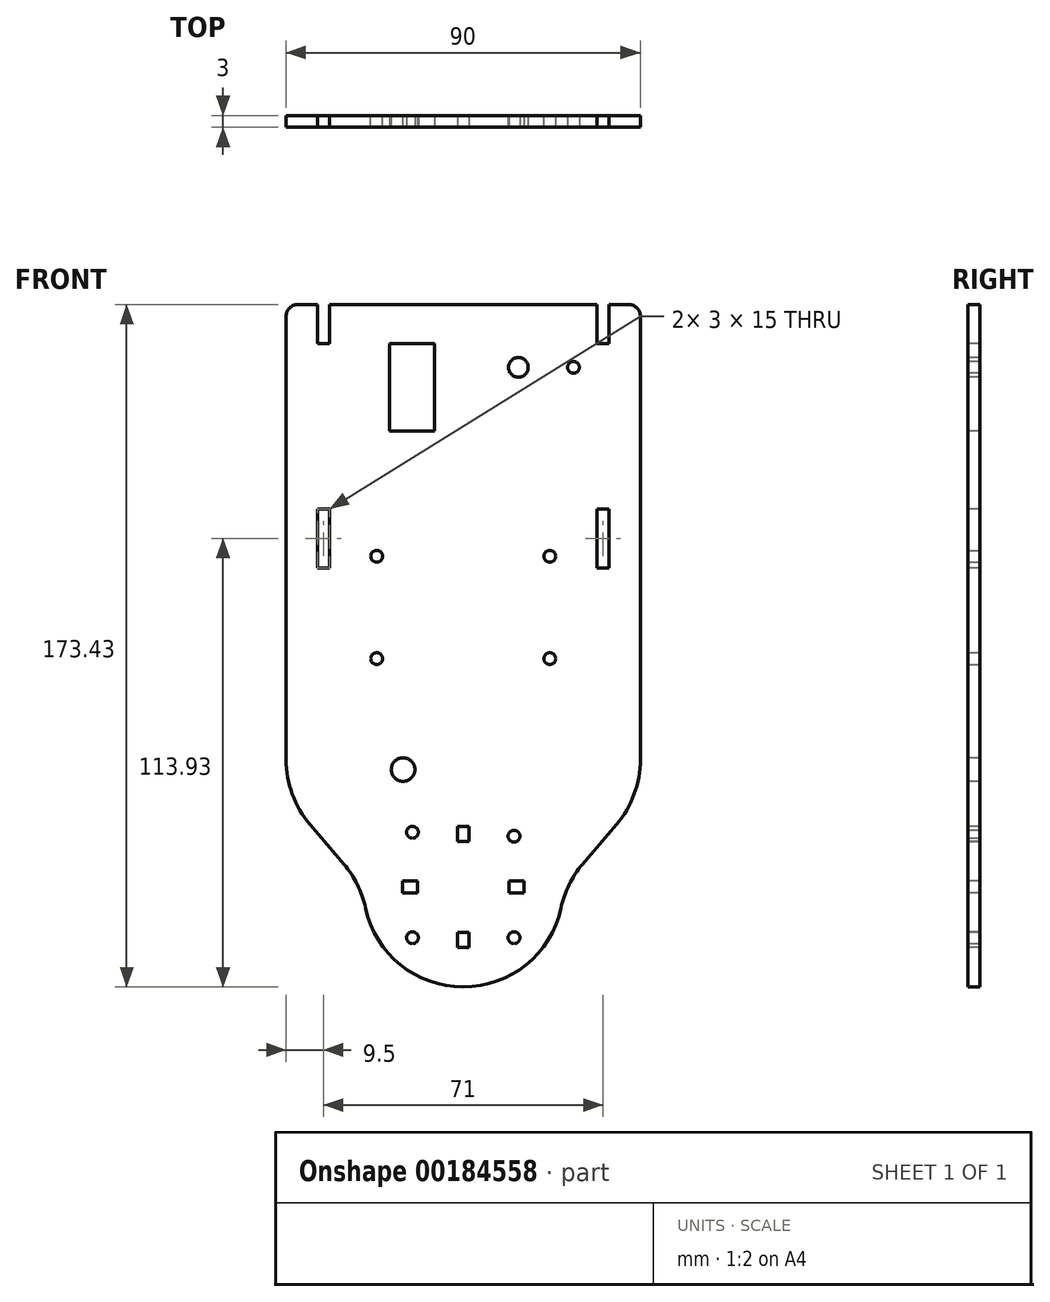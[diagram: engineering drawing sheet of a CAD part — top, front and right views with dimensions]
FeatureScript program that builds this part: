
annotation { "Feature Type Name" : "Feature", "Feature Type Description" : "" }
export const myFeature = defineFeature(function(context is Context, id is Id, definition is map)
    precondition{}
    {
        {
            var Q0;
            Q0=qCreatedBy(makeId("Front.planeOp"),FACE);
            var sketch = newSketch(context, id + "F0", { "sketchPlane" : qUnion([Q0])});
            skLineSegment(sketch, "E0.bottom", {"start": v(0, 0) * mm, "end": v(-90, 0) * mm});
            skLineSegment(sketch, "E0.top", {"start": v(0, 125) * mm, "end": v(-90, 125) * mm});
            skLineSegment(sketch, "E0.left", {"start": v(0, 0) * mm, "end": v(0, 125) * mm});
            skLineSegment(sketch, "E0.right", {"start": v(-90, 0) * mm, "end": v(-90, 125) * mm});
            skLineSegment(sketch, "E1", {"start": v(-90, 0) * mm, "end": v(-45, -70) * mm});
            skLineSegment(sketch, "E2", {"start": v(-45, -70) * mm, "end": v(0, 0) * mm});
            skSolve(sketch);
        }
        {
            var Q0;
            Q0=makeQuery(id+"F0.imprint","IMPRINT",FACE,{"disambiguationData":[TD([[makeQuery(id+"F0.imprint","IMPRINT",EDGE,{"derivedFrom":sQuery(id+"F0.wireOp",EDGE,"E0.bottom")}),-1.0]])]});
            var Q1;
            Q1=makeQuery(id+"F0.imprint","IMPRINT",FACE,{"disambiguationData":[TD([[makeQuery(id+"F0.imprint","IMPRINT",EDGE,{"derivedFrom":sQuery(id+"F0.wireOp",EDGE,"E0.bottom")}),1.0]])]});
            extrude(context, id + "F1", {"entities" : qUnion([Q0, Q1]), "depth" : 3 * mm});
        }
        {
            var Q0;
            Q0=makeQuery(id+"F1.opExtrude","CAP_FACE",FACE,{"disambiguationData":[OSD([sQuery(id+"F0.wireOp",EDGE,"E0.top"),sQuery(id+"F0.wireOp",EDGE,"E0.left"),sQuery(id+"F0.wireOp",EDGE,"E0.right"),sQuery(id+"F0.wireOp",EDGE,"E1"),sQuery(id+"F0.wireOp",EDGE,"E2")])],"isStart":false});
            var sketch = newSketch(context, id + "F2", { "sketchPlane" : qUnion([Q0])});
            skLineSegment(sketch, "E3.bottom", {"start": v(-8, 130) * mm, "end": v(-11, 130) * mm});
            skLineSegment(sketch, "E3.top", {"start": v(-8, 115) * mm, "end": v(-11, 115) * mm});
            skLineSegment(sketch, "E3.left", {"start": v(-11, 130) * mm, "end": v(-11, 115) * mm});
            skLineSegment(sketch, "E3.right", {"start": v(-8, 130) * mm, "end": v(-8, 115) * mm});
            skLineSegment(sketch, "E4.bottom", {"start": v(-8, 73) * mm, "end": v(-11, 73) * mm});
            skLineSegment(sketch, "E4.top", {"start": v(-8, 58) * mm, "end": v(-11, 58) * mm});
            skLineSegment(sketch, "E4.left", {"start": v(-8, 73) * mm, "end": v(-8, 58) * mm});
            skLineSegment(sketch, "E4.right", {"start": v(-11, 73) * mm, "end": v(-11, 58) * mm});
            skLineSegment(sketch, "E5.bottom", {"start": v(-79, 130) * mm, "end": v(-82, 130) * mm});
            skLineSegment(sketch, "E5.top", {"start": v(-79, 115) * mm, "end": v(-82, 115) * mm});
            skLineSegment(sketch, "E5.left", {"start": v(-79, 130) * mm, "end": v(-79, 115) * mm});
            skLineSegment(sketch, "E5.right", {"start": v(-82, 130) * mm, "end": v(-82, 115) * mm});
            skLineSegment(sketch, "E6.bottom", {"start": v(-79, 73) * mm, "end": v(-82, 73) * mm});
            skLineSegment(sketch, "E6.top", {"start": v(-79, 58) * mm, "end": v(-82, 58) * mm});
            skLineSegment(sketch, "E6.left", {"start": v(-79, 73) * mm, "end": v(-79, 58) * mm});
            skLineSegment(sketch, "E6.right", {"start": v(-82, 73) * mm, "end": v(-82, 58) * mm});
            skLineSegment(sketch, "E7", {"start": v(-79, 58) * mm, "end": v(-11, 58) * mm});
            skLineSegment(sketch, "E8.bottom", {"start": v(-40, 58) * mm, "end": v(-35, 58) * mm});
            skLineSegment(sketch, "E8.top", {"start": v(-40, 55) * mm, "end": v(-35, 55) * mm});
            skLineSegment(sketch, "E8.left", {"start": v(-40, 58) * mm, "end": v(-40, 55) * mm});
            skLineSegment(sketch, "E8.right", {"start": v(-35, 58) * mm, "end": v(-35, 55) * mm});
            skLineSegment(sketch, "E9", {"start": v(-45, 58) * mm, "end": v(-45, 63.12) * mm});
            skPoint(sketch, "E9.endSnap0", {"position": v(-45, 58) * mm});
            skLineSegment(sketch, "E10.bottom", {"start": v(-50, 58) * mm, "end": v(-55, 58) * mm});
            skLineSegment(sketch, "E10.top", {"start": v(-50, 55) * mm, "end": v(-55, 55) * mm});
            skLineSegment(sketch, "E10.left", {"start": v(-50, 58) * mm, "end": v(-50, 55) * mm});
            skLineSegment(sketch, "E10.right", {"start": v(-55, 58) * mm, "end": v(-55, 55) * mm});
            skSolve(sketch);
        }
        {
            var Q0;
            Q0=makeQuery(id+"F1.opExtrude","CAP_FACE",FACE,{"disambiguationData":[OSD([sQuery(id+"F0.wireOp",EDGE,"E0.top"),sQuery(id+"F0.wireOp",EDGE,"E0.left"),sQuery(id+"F0.wireOp",EDGE,"E0.right"),sQuery(id+"F0.wireOp",EDGE,"E1"),sQuery(id+"F0.wireOp",EDGE,"E2")])],"isStart":false});
            var sketch = newSketch(context, id + "F3", { "sketchPlane" : qUnion([Q0])});
            skLineSegment(sketch, "E11.bottom", {"start": v(-63.75, 115) * mm, "end": v(-52.25, 115) * mm});
            skLineSegment(sketch, "E11.top", {"start": v(-63.75, 92.8) * mm, "end": v(-52.25, 92.8) * mm});
            skLineSegment(sketch, "E11.left", {"start": v(-63.75, 115) * mm, "end": v(-63.75, 92.8) * mm});
            skLineSegment(sketch, "E11.right", {"start": v(-52.25, 115) * mm, "end": v(-52.25, 92.8) * mm});
            skCircle(sketch, "E12", {"center": v(-58, 117) * mm, "radius": 1 * mm});
            skCircle(sketch, "E13", {"center": v(-58, 90.8) * mm, "radius": 1 * mm});
            skLineSegment(sketch, "E14", {"start": v(-59, 117) * mm, "end": v(-59, 115) * mm});
            skLineSegment(sketch, "E15", {"start": v(-57, 117) * mm, "end": v(-57, 115) * mm});
            skLineSegment(sketch, "E16", {"start": v(-59, 90.8) * mm, "end": v(-59, 92.8) * mm});
            skLineSegment(sketch, "E17", {"start": v(-57, 92.8) * mm, "end": v(-57, 90.8) * mm});
            skLineSegment(sketch, "E18", {"start": v(-45, 125) * mm, "end": v(-45, -52.75) * mm});
            skLineSegment(sketch, "E19", {"start": v(-58, 115) * mm, "end": v(-58, 92.8) * mm});
            skLineSegment(sketch, "E20", {"start": v(-63.75, 109) * mm, "end": v(-52.25, 109) * mm});
            skCircle(sketch, "E21", {"center": v(-31, 109) * mm, "radius": 2.5 * mm});
            skCircle(sketch, "E22", {"center": v(-17, 109) * mm, "radius": 1.5 * mm});
            skSolve(sketch);
        }
        {
            var Q0;
            {var subQ0=sQuery(id+"F3.wireOp",EDGE,"E11.left");Q0=makeQuery(id+"F3.imprint","IMPRINT",FACE,{"disambiguationData":[TD([[makeQuery(id+"F3.imprint","IMPRINT",EDGE,{"derivedFrom":subQ0}),1.0]])]});}
            var Q1;
            {var subQ1=sQuery(id+"F3.wireOp",EDGE,"E11.bottom");var subQ8=makeQuery(id+"F3.imprint","INTERSECT",VERTEX,{"derivedFrom":[subQ1,sQuery(id+"F3.wireOp",EDGE,"E15")]});Q1=makeQuery(id+"F3.imprint","IMPRINT",FACE,{"disambiguationData":[TD([[makeQuery(id+"F3.imprint","IMPRINT",EDGE,{"disambiguationData":[TD([[subQ8,1.0]])],"derivedFrom":subQ1}),-1.0]])]});}
            var Q2;
            {var subQ1=sQuery(id+"F3.wireOp",EDGE,"E11.top");var subQ7=makeQuery(id+"F3.imprint","INTERSECT",VERTEX,{"derivedFrom":[subQ1,sQuery(id+"F3.wireOp",EDGE,"E17")]});Q2=makeQuery(id+"F3.imprint","IMPRINT",FACE,{"disambiguationData":[TD([[makeQuery(id+"F3.imprint","IMPRINT",EDGE,{"disambiguationData":[TD([[subQ7,1.0]])],"derivedFrom":subQ1}),1.0]])]});}
            var Q3;
            Q3=makeQuery(id+"F3.imprint","IMPRINT",FACE,{"disambiguationData":[TD([[makeQuery(id+"F3.imprint","IMPRINT",EDGE,{"derivedFrom":sQuery(id+"F3.wireOp",EDGE,"E21")}),1.0]])]});
            var Q4;
            Q4=makeQuery(id+"F3.imprint","IMPRINT",FACE,{"disambiguationData":[TD([[makeQuery(id+"F3.imprint","IMPRINT",EDGE,{"derivedFrom":sQuery(id+"F3.wireOp",EDGE,"E22")}),1.0]])]});
            extrude(context, id + "F4", {"entities" : qUnion([Q0, Q1, Q2, Q3, Q4]), "operationType" : NewBodyOperationType.REMOVE, "oppositeDirection" : true, "depth" : 25.4 * mm});
        }
        {
            var Q0;
            Q0=makeQuery(id+"F1.opExtrude","SWEPT_EDGE",EDGE,{"disambiguationData":[OSD([sQuery(id+"F0.wireOp",EDGE,"E1"),sQuery(id+"F0.wireOp",EDGE,"E2")])]});
            fillet(context, id + "F5", {"entities" : qUnion([Q0]), "radius" : 25.4 * mm, "tangentPropagation" : true, "allowEdgeOverflow" : false});
        }
        {
            var Q0;
            Q0=makeQuery(id+"F2.imprint","IMPRINT",FACE,{"disambiguationData":[TD([[makeQuery(id+"F2.imprint","IMPRINT",EDGE,{"derivedFrom":sQuery(id+"F2.wireOp",EDGE,"E5.bottom")}),1.0]])]});
            var Q1;
            Q1=makeQuery(id+"F2.imprint","IMPRINT",FACE,{"disambiguationData":[TD([[makeQuery(id+"F2.imprint","IMPRINT",EDGE,{"derivedFrom":sQuery(id+"F2.wireOp",EDGE,"E3.bottom")}),1.0]])]});
            var Q2;
            Q2=makeQuery(id+"F2.imprint","IMPRINT",FACE,{"disambiguationData":[TD([[makeQuery(id+"F2.imprint","IMPRINT",EDGE,{"derivedFrom":sQuery(id+"F2.wireOp",EDGE,"E4.bottom")}),1.0]])]});
            var Q3;
            Q3=makeQuery(id+"F2.imprint","IMPRINT",FACE,{"disambiguationData":[TD([[makeQuery(id+"F2.imprint","IMPRINT",EDGE,{"derivedFrom":sQuery(id+"F2.wireOp",EDGE,"E6.bottom")}),1.0]])]});
            var Q4;
            {var subQ0=sQuery(id+"F2.wireOp",EDGE,"E5.top");Q4=makeQuery(id+"F2.imprint","IMPRINT",FACE,{"disambiguationData":[TD([[makeQuery(id+"F2.imprint","IMPRINT",EDGE,{"derivedFrom":subQ0}),-1.0]])]});}
            var Q5;
            {var subQ0=sQuery(id+"F2.wireOp",EDGE,"E3.top");Q5=makeQuery(id+"F2.imprint","IMPRINT",FACE,{"disambiguationData":[TD([[makeQuery(id+"F2.imprint","IMPRINT",EDGE,{"derivedFrom":subQ0}),-1.0]])]});}
            var Q6;
            Q6=makeQuery(id+"F2.imprint","IMPRINT",FACE,{"disambiguationData":[TD([[makeQuery(id+"F2.imprint","IMPRINT",EDGE,{"derivedFrom":sQuery(id+"F2.wireOp",EDGE,"E10.bottom")}),1.0]])]});
            var Q7;
            Q7=makeQuery(id+"F2.imprint","IMPRINT",FACE,{"disambiguationData":[TD([[makeQuery(id+"F2.imprint","IMPRINT",EDGE,{"derivedFrom":sQuery(id+"F2.wireOp",EDGE,"E8.bottom")}),-1.0]])]});
            extrude(context, id + "F6", {"entities" : qUnion([Q0, Q1, Q2, Q3, Q4, Q5, Q6, Q7]), "operationType" : NewBodyOperationType.REMOVE, "oppositeDirection" : true, "depth" : 25.4 * mm});
        }
        {
            var Q0;
            Q0=makeQuery(id+"F1.opExtrude","CAP_FACE",FACE,{"disambiguationData":[OSD([sQuery(id+"F0.wireOp",EDGE,"E0.top"),sQuery(id+"F0.wireOp",EDGE,"E0.left"),sQuery(id+"F0.wireOp",EDGE,"E0.right"),sQuery(id+"F0.wireOp",EDGE,"E1"),sQuery(id+"F0.wireOp",EDGE,"E2")])],"isStart":false});
            var sketch = newSketch(context, id + "F7", { "sketchPlane" : qUnion([Q0])});
            skCircle(sketch, "E23", {"center": v(-45, -23.03) * mm, "radius": 25.4 * mm});
            skLineSegment(sketch, "E24", {"start": v(-45, -48.43) * mm, "end": v(-45, 2.37) * mm});
            skLineSegment(sketch, "E25", {"start": v(-45, -23.03) * mm, "end": v(-19.6, -23.03) * mm});
            skLineSegment(sketch, "E26", {"start": v(-45, -23.03) * mm, "end": v(-70.4, -23.03) * mm});
            skLineSegment(sketch, "E27.bottom", {"start": v(-60.4, -24.53) * mm, "end": v(-56.59, -24.53) * mm});
            skLineSegment(sketch, "E27.top", {"start": v(-60.4, -21.53) * mm, "end": v(-56.59, -21.53) * mm});
            skLineSegment(sketch, "E27.left", {"start": v(-60.4, -24.53) * mm, "end": v(-60.4, -21.53) * mm});
            skLineSegment(sketch, "E27.right", {"start": v(-56.59, -24.53) * mm, "end": v(-56.59, -21.53) * mm});
            skLineSegment(sketch, "E28.bottom", {"start": v(-46.5, -11.44) * mm, "end": v(-43.5, -11.44) * mm});
            skLineSegment(sketch, "E28.top", {"start": v(-46.5, -7.63) * mm, "end": v(-43.5, -7.63) * mm});
            skLineSegment(sketch, "E28.left", {"start": v(-46.5, -11.44) * mm, "end": v(-46.5, -7.63) * mm});
            skLineSegment(sketch, "E28.right", {"start": v(-43.5, -11.44) * mm, "end": v(-43.5, -7.63) * mm});
            skLineSegment(sketch, "E29.bottom", {"start": v(-33.4, -21.53) * mm, "end": v(-29.6, -21.53) * mm});
            skLineSegment(sketch, "E29.top", {"start": v(-33.4, -24.53) * mm, "end": v(-29.6, -24.53) * mm});
            skLineSegment(sketch, "E29.left", {"start": v(-33.4, -21.53) * mm, "end": v(-33.4, -24.53) * mm});
            skLineSegment(sketch, "E29.right", {"start": v(-29.6, -21.53) * mm, "end": v(-29.6, -24.53) * mm});
            skLineSegment(sketch, "E30.bottom", {"start": v(-46.5, -34.62) * mm, "end": v(-43.5, -34.62) * mm});
            skLineSegment(sketch, "E30.top", {"start": v(-46.5, -38.43) * mm, "end": v(-43.5, -38.43) * mm});
            skLineSegment(sketch, "E30.left", {"start": v(-46.5, -34.62) * mm, "end": v(-46.5, -38.43) * mm});
            skLineSegment(sketch, "E30.right", {"start": v(-43.5, -34.62) * mm, "end": v(-43.5, -38.43) * mm});
            skLineSegment(sketch, "E31", {"start": v(-45, -3.98) * mm, "end": v(-45, -11.44) * mm});
            skCircle(sketch, "E32", {"center": v(-57.9, -9.13) * mm, "radius": 1.5 * mm});
            skCircle(sketch, "E33", {"center": v(-32.1, -10.13) * mm, "radius": 1.5 * mm});
            skCircle(sketch, "E34", {"center": v(-32.1, -35.93) * mm, "radius": 1.5 * mm});
            skCircle(sketch, "E35", {"center": v(-57.9, -35.93) * mm, "radius": 1.5 * mm});
            skSolve(sketch);
        }
        {
            var Q0;
            {var subQ5=sQuery(id+"F7.wireOp",EDGE,"E27.top");Q0=makeQuery(id+"F7.imprint","IMPRINT",FACE,{"disambiguationData":[TD([[makeQuery(id+"F7.imprint","IMPRINT",EDGE,{"derivedFrom":subQ5}),-1.0]])]});}
            var Q1;
            {var subQ5=sQuery(id+"F7.wireOp",EDGE,"E27.bottom");Q1=makeQuery(id+"F7.imprint","IMPRINT",FACE,{"disambiguationData":[TD([[makeQuery(id+"F7.imprint","IMPRINT",EDGE,{"derivedFrom":subQ5}),1.0]])]});}
            var Q2;
            {var subQ5=sQuery(id+"F7.wireOp",EDGE,"E29.bottom");Q2=makeQuery(id+"F7.imprint","IMPRINT",FACE,{"disambiguationData":[TD([[makeQuery(id+"F7.imprint","IMPRINT",EDGE,{"derivedFrom":subQ5}),-1.0]])]});}
            var Q3;
            {var subQ5=sQuery(id+"F7.wireOp",EDGE,"E29.top");Q3=makeQuery(id+"F7.imprint","IMPRINT",FACE,{"disambiguationData":[TD([[makeQuery(id+"F7.imprint","IMPRINT",EDGE,{"derivedFrom":subQ5}),1.0]])]});}
            var Q4;
            {var subQ5=sQuery(id+"F7.wireOp",EDGE,"E30.right");Q4=makeQuery(id+"F7.imprint","IMPRINT",FACE,{"disambiguationData":[TD([[makeQuery(id+"F7.imprint","IMPRINT",EDGE,{"derivedFrom":subQ5}),-1.0]])]});}
            var Q5;
            {var subQ5=sQuery(id+"F7.wireOp",EDGE,"E30.left");Q5=makeQuery(id+"F7.imprint","IMPRINT",FACE,{"disambiguationData":[TD([[makeQuery(id+"F7.imprint","IMPRINT",EDGE,{"derivedFrom":subQ5}),1.0]])]});}
            var Q6;
            {var subQ5=sQuery(id+"F7.wireOp",EDGE,"E28.right");Q6=makeQuery(id+"F7.imprint","IMPRINT",FACE,{"disambiguationData":[TD([[makeQuery(id+"F7.imprint","IMPRINT",EDGE,{"derivedFrom":subQ5}),1.0]])]});}
            var Q7;
            {var subQ5=sQuery(id+"F7.wireOp",EDGE,"E28.left");Q7=makeQuery(id+"F7.imprint","IMPRINT",FACE,{"disambiguationData":[TD([[makeQuery(id+"F7.imprint","IMPRINT",EDGE,{"derivedFrom":subQ5}),-1.0]])]});}
            var Q8;
            {var subQ5=sQuery(id+"F7.wireOp",EDGE,"Zrzo9GHM-fuN2-8fML-iVZU-LCXHQRcVOfyt.left");Q8=makeQuery(id+"F7.imprint","IMPRINT",FACE,{"disambiguationData":[TD([[makeQuery(id+"F7.imprint","IMPRINT",EDGE,{"derivedFrom":subQ5}),1.0]])]});}
            var Q9;
            {var subQ5=sQuery(id+"F7.wireOp",EDGE,"Zrzo9GHM-fuN2-8fML-iVZU-LCXHQRcVOfyt.right");Q9=makeQuery(id+"F7.imprint","IMPRINT",FACE,{"disambiguationData":[TD([[makeQuery(id+"F7.imprint","IMPRINT",EDGE,{"derivedFrom":subQ5}),-1.0]])]});}
            var Q10;
            {var subQ0=sQuery(id+"F7.wireOp",EDGE,"2EuhVOSW-e1DR-vE8P-bMp6-yslpzd3IsdpB");var subQ4=makeQuery(id+"F7.imprint","IMPRINT",VERTEX,{"derivedFrom":subQ0});Q10=makeQuery(id+"F7.imprint","IMPRINT",FACE,{"disambiguationData":[TD([[makeQuery(id+"F7.imprint","IMPRINT",EDGE,{"disambiguationData":[TD([[subQ4,1.0]])],"derivedFrom":subQ0}),-1.0]])]});}
            var Q11;
            {var subQ0=sQuery(id+"F7.wireOp",EDGE,"2EuhVOSW-e1DR-vE8P-bMp6-yslpzd3IsdpB");var subQ4=makeQuery(id+"F7.imprint","IMPRINT",VERTEX,{"derivedFrom":subQ0});Q11=makeQuery(id+"F7.imprint","IMPRINT",FACE,{"disambiguationData":[TD([[makeQuery(id+"F7.imprint","IMPRINT",EDGE,{"disambiguationData":[TD([[subQ4,1.0]])],"derivedFrom":subQ0}),1.0]])]});}
            var Q12;
            Q12=makeQuery(id+"F7.imprint","IMPRINT",FACE,{"disambiguationData":[TD([[makeQuery(id+"F7.imprint","IMPRINT",EDGE,{"derivedFrom":sQuery(id+"F7.wireOp",EDGE,"E32")}),1.0]])]});
            var Q13;
            Q13=makeQuery(id+"F7.imprint","IMPRINT",FACE,{"disambiguationData":[TD([[makeQuery(id+"F7.imprint","IMPRINT",EDGE,{"derivedFrom":sQuery(id+"F7.wireOp",EDGE,"E33")}),1.0]])]});
            var Q14;
            Q14=makeQuery(id+"F7.imprint","IMPRINT",FACE,{"disambiguationData":[TD([[makeQuery(id+"F7.imprint","IMPRINT",EDGE,{"derivedFrom":sQuery(id+"F7.wireOp",EDGE,"E34")}),1.0]])]});
            var Q15;
            Q15=makeQuery(id+"F7.imprint","IMPRINT",FACE,{"disambiguationData":[TD([[makeQuery(id+"F7.imprint","IMPRINT",EDGE,{"derivedFrom":sQuery(id+"F7.wireOp",EDGE,"E35")}),1.0]])]});
            extrude(context, id + "F8", {"entities" : qUnion([Q0, Q1, Q2, Q3, Q4, Q5, Q6, Q7, Q8, Q9, Q10, Q11, Q12, Q13, Q14, Q15]), "operationType" : NewBodyOperationType.REMOVE, "oppositeDirection" : true, "depth" : 25.4 * mm});
        }
        {
            var Q0;
            Q0=makeQuery(id+"F1.opExtrude","SWEPT_EDGE",EDGE,{"disambiguationData":[OSD([sQuery(id+"F0.wireOp",EDGE,"E0.top"),sQuery(id+"F0.wireOp",EDGE,"E0.left")])]});
            var Q1;
            Q1=makeQuery(id+"F1.opExtrude","SWEPT_EDGE",EDGE,{"disambiguationData":[OSD([sQuery(id+"F0.wireOp",EDGE,"E0.top"),sQuery(id+"F0.wireOp",EDGE,"E0.right")])]});
            fillet(context, id + "F9", {"entities" : qUnion([Q0, Q1]), "radius" : 3 * mm, "tangentPropagation" : true, "allowEdgeOverflow" : false});
        }
        {
            var Q0;
            Q0=makeQuery(id+"F1.opExtrude","CAP_FACE",FACE,{"disambiguationData":[OSD([sQuery(id+"F0.wireOp",EDGE,"E0.top"),sQuery(id+"F0.wireOp",EDGE,"E0.left"),sQuery(id+"F0.wireOp",EDGE,"E0.right"),sQuery(id+"F0.wireOp",EDGE,"E1"),sQuery(id+"F0.wireOp",EDGE,"E2")])],"isStart":false});
            var sketch = newSketch(context, id + "F10", { "sketchPlane" : qUnion([Q0])});
            skCircle(sketch, "E36", {"center": v(-45, -23.03) * mm, "radius": 25.4 * mm});
            skLineSegment(sketch, "E37", {"start": v(-45, -23.03) * mm, "end": v(-70.4, -23.03) * mm});
            skLineSegment(sketch, "E38", {"start": v(-45, -23.03) * mm, "end": v(-19.6, -23.03) * mm});
            skLineSegment(sketch, "E39", {"start": v(-70.4, -23.03) * mm, "end": v(-90, 0) * mm});
            skLineSegment(sketch, "E40", {"start": v(-19.6, -23.03) * mm, "end": v(0, 0) * mm});
            skSolve(sketch);
        }
        {
            var Q0;
            {var subQ2=sQuery(id+"F10.wireOp",EDGE,"E39");Q0=makeQuery(id+"F10.imprint","IMPRINT",FACE,{"disambiguationData":[TD([[makeQuery(id+"F10.imprint","IMPRINT",EDGE,{"derivedFrom":subQ2}),1.0]])]});}
            var Q1;
            {var subQ2=sQuery(id+"F10.wireOp",EDGE,"E40");Q1=makeQuery(id+"F10.imprint","IMPRINT",FACE,{"disambiguationData":[TD([[makeQuery(id+"F10.imprint","IMPRINT",EDGE,{"derivedFrom":subQ2}),-1.0]])]});}
            extrude(context, id + "F11", {"entities" : qUnion([Q0, Q1]), "operationType" : NewBodyOperationType.REMOVE, "oppositeDirection" : true, "depth" : 25.4 * mm});
        }
        {
            var Q0;
            Q0=makeQuery(id+"F11.boolean.opBoolean","COPY",EDGE,{"derivedFrom":makeQuery(id+"F11.opExtrude","SWEPT_EDGE",EDGE,{"disambiguationData":[OSD([sQuery(id+"F10.wireOp",EDGE,"E36"),sQuery(id+"F10.wireOp",EDGE,"E37"),sQuery(id+"F10.wireOp",EDGE,"E39")])]})});
            var Q1;
            {var subQ0=sQuery(id+"F0.wireOp",EDGE,"E1");var subQ1=sQuery(id+"F0.wireOp",EDGE,"E0.right");Q1=makeQuery(id+"F11.boolean.opBoolean","MERGE",EDGE,{"derivedFrom":[makeQuery(id+"F1.opExtrude","SWEPT_EDGE",EDGE,{"disambiguationData":[OSD([sQuery(id+"F0.wireOp",EDGE,"E0.bottom"),subQ1,subQ0])]}),makeQuery(id+"F11.opExtrude","SWEPT_EDGE",EDGE,{"disambiguationData":[OSD([subQ1,subQ0,sQuery(id+"F10.wireOp",EDGE,"E39")])]})]});}
            var Q2;
            Q2=makeQuery(id+"F11.boolean.opBoolean","COPY",EDGE,{"derivedFrom":makeQuery(id+"F11.opExtrude","SWEPT_EDGE",EDGE,{"disambiguationData":[OSD([sQuery(id+"F10.wireOp",EDGE,"E36"),sQuery(id+"F10.wireOp",EDGE,"E38"),sQuery(id+"F10.wireOp",EDGE,"E40")])]})});
            var Q3;
            {var subQ0=sQuery(id+"F0.wireOp",EDGE,"E2");var subQ1=sQuery(id+"F0.wireOp",EDGE,"E0.left");Q3=makeQuery(id+"F11.boolean.opBoolean","MERGE",EDGE,{"derivedFrom":[makeQuery(id+"F1.opExtrude","SWEPT_EDGE",EDGE,{"disambiguationData":[OSD([sQuery(id+"F0.wireOp",EDGE,"E0.bottom"),subQ1,subQ0])]}),makeQuery(id+"F11.opExtrude","SWEPT_EDGE",EDGE,{"disambiguationData":[OSD([subQ1,subQ0,sQuery(id+"F10.wireOp",EDGE,"E40")])]})]});}
            fillet(context, id + "F12", {"entities" : qUnion([Q0, Q1, Q2, Q3]), "radius" : 25.4 * mm, "tangentPropagation" : true, "allowEdgeOverflow" : false});
        }
        {
            var Q0;
            Q0=makeQuery(id+"F1.opExtrude","CAP_FACE",FACE,{"disambiguationData":[OSD([sQuery(id+"F0.wireOp",EDGE,"E0.top"),sQuery(id+"F0.wireOp",EDGE,"E0.left"),sQuery(id+"F0.wireOp",EDGE,"E0.right"),sQuery(id+"F0.wireOp",EDGE,"E1"),sQuery(id+"F0.wireOp",EDGE,"E2")])],"isStart":true});
            var sketch = newSketch(context, id + "F13", { "sketchPlane" : qUnion([Q0])});
            skLineSegment(sketch, "E41", {"start": v(0, 82.15) * mm, "end": v(90, 82.15) * mm, "construction": true});
            skLineSegment(sketch, "E42", {"start": v(45, 82.15) * mm, "end": v(45, 25.97) * mm, "construction": true});
            skCircle(sketch, "E43", {"center": v(23, 61) * mm, "radius": 1.5 * mm});
            skCircle(sketch, "E44.MirrorC", {"center": v(23, 35) * mm, "radius": 1.5 * mm});
            skCircle(sketch, "E45.MirrorC", {"center": v(67, 35) * mm, "radius": 1.5 * mm});
            skCircle(sketch, "E46.MirrorC", {"center": v(67, 61) * mm, "radius": 1.5 * mm});
            skLineSegment(sketch, "E47", {"start": v(35, 58) * mm, "end": v(11, 58) * mm, "construction": true});
            skSolve(sketch);
        }
        {
            var Q0;
            Q0=qSketchRegion(id+"F13",true);
            extrude(context, id + "F14", {"entities" : qUnion([Q0]), "operationType" : NewBodyOperationType.REMOVE, "endBound" : BoundingType.UP_TO_NEXT, "oppositeDirection" : true, "depth" : 25 * mm});
        }
        {
            var Q0;
            Q0=makeQuery(id+"F1.opExtrude","CAP_FACE",FACE,{"disambiguationData":[OSD([sQuery(id+"F0.wireOp",EDGE,"E0.top"),sQuery(id+"F0.wireOp",EDGE,"E0.left"),sQuery(id+"F0.wireOp",EDGE,"E0.right"),sQuery(id+"F0.wireOp",EDGE,"E1"),sQuery(id+"F0.wireOp",EDGE,"E2")])],"isStart":false});
            var sketch = newSketch(context, id + "F15", { "sketchPlane" : qUnion([Q0])});
            skLineSegment(sketch, "E48", {"start": v(-89.87, 6.8) * mm, "end": v(-60.3, 6.8) * mm});
            skCircle(sketch, "E49", {"center": v(-60.3, 6.8) * mm, "radius": 3 * mm});
            skSolve(sketch);
        }
        {
            var Q0;
            Q0=makeQuery(id+"F15.imprint","IMPRINT",FACE,{"disambiguationData":[TD([[makeQuery(id+"F15.imprint","IMPRINT",EDGE,{"derivedFrom":sQuery(id+"F15.wireOp",EDGE,"E49")}),1.0]])]});
            extrude(context, id + "F16", {"entities" : qUnion([Q0]), "operationType" : NewBodyOperationType.REMOVE, "oppositeDirection" : true, "depth" : 3 * mm});
        }
    });
